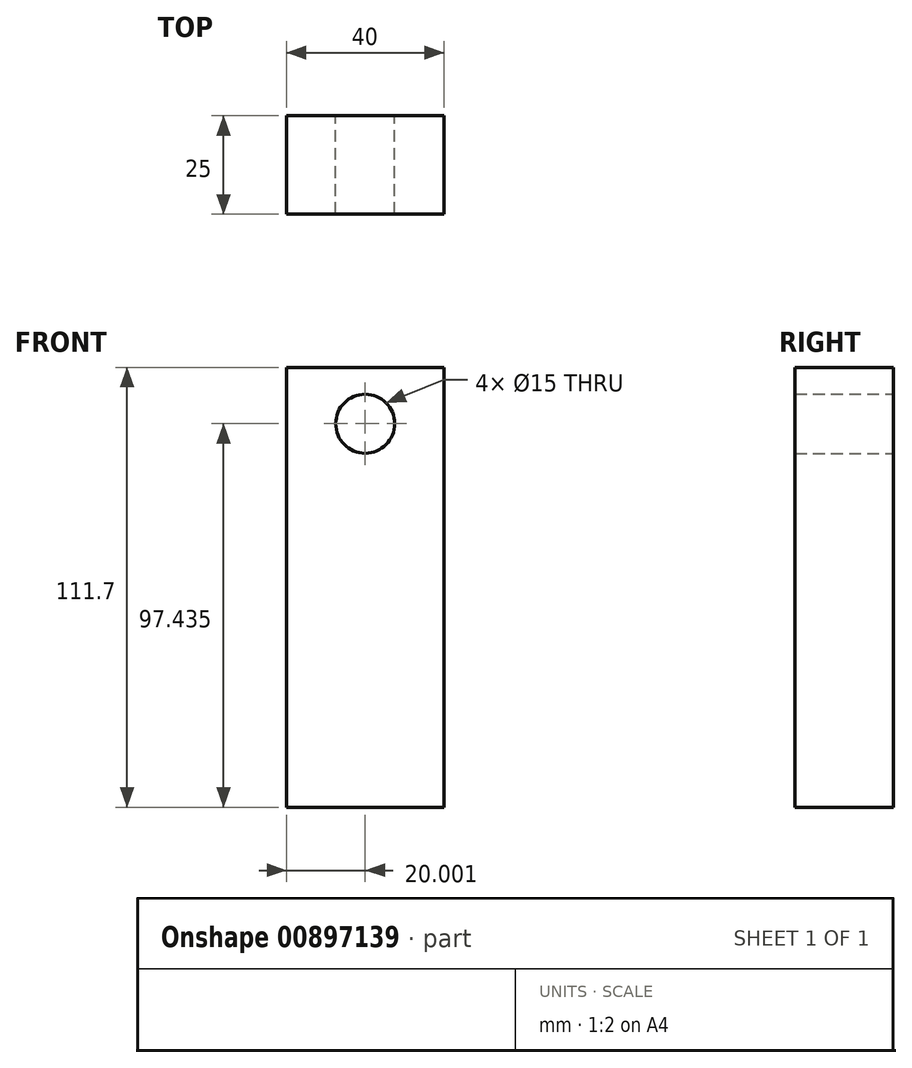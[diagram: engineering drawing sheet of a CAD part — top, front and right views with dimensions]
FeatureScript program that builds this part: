
annotation { "Feature Type Name" : "Feature", "Feature Type Description" : "" }
export const myFeature = defineFeature(function(context is Context, id is Id, definition is map)
    precondition{}
    {
        {
            var Q0;
            Q0=qCreatedBy(makeId("Front.planeOp"),FACE);
            var sketch = newSketch(context, id + "F0", { "sketchPlane" : qUnion([Q0])});
            skLineSegment(sketch, "E0.bottom", {"start": v(-36, 53.84) * mm, "end": v(4, 53.84) * mm});
            skLineSegment(sketch, "E0.top", {"start": v(-36, -57.86) * mm, "end": v(4, -57.86) * mm});
            skLineSegment(sketch, "E0.left", {"start": v(-36, 53.84) * mm, "end": v(-36, -57.86) * mm});
            skLineSegment(sketch, "E0.right", {"start": v(4, 53.84) * mm, "end": v(4, -57.86) * mm});
            skLineSegment(sketch, "E1", {"start": v(4, -67.44) * mm, "end": v(-16, -67.44) * mm});
            skCircle(sketch, "E2", {"center": v(-16, 39.58) * mm, "radius": 7.5 * mm});
            skSolve(sketch);
        }
        {
            var Q0;
            Q0=makeQuery(id+"F0.imprint","IMPRINT",FACE,{"disambiguationData":[TD([[makeQuery(id+"F0.imprint","IMPRINT",EDGE,{"derivedFrom":sQuery(id+"F0.wireOp",EDGE,"E0.bottom")}),-1.0]])]});
            extrude(context, id + "F1", {"entities" : qUnion([Q0]), "depth" : 25 * mm, "offsetDistance" : 25 * mm});
        }
    });
